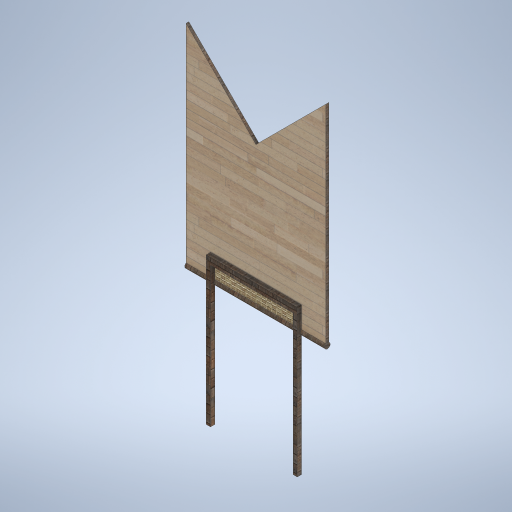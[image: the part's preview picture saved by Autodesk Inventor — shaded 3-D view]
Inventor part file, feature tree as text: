
AUTODESK INVENTOR PART (.ipt)
format: ipt  version: 2024.2 (Build 282272000, 272)  size: 369,152 bytes
history: native  units: mm
features: extrude x5, sketch x4, other x1
ambient origin geometry x8: Origin, YZ Plane, XZ Plane, XY Plane, X Axis, Y Axis, Z Axis, Center Point
bodies: Body1 (feature_tree)
feature tree (10):
  other  "實體1"
  extrude  "擠出1"  Depth=1500.0mm
  extrude  "擠出2"  Depth=1000.0mm
  extrude  "擠出3"  Depth=20.0mm TaperAngle=0.0deg
  sketch  "草圖4"
  extrude  "擠出4"  Depth=40.0mm
  extrude  "擠出5"  Depth=1000.0mm TaperAngle=0.0deg
  sketch  "草圖1"
  sketch  "草圖2"
  sketch  "草圖3"
